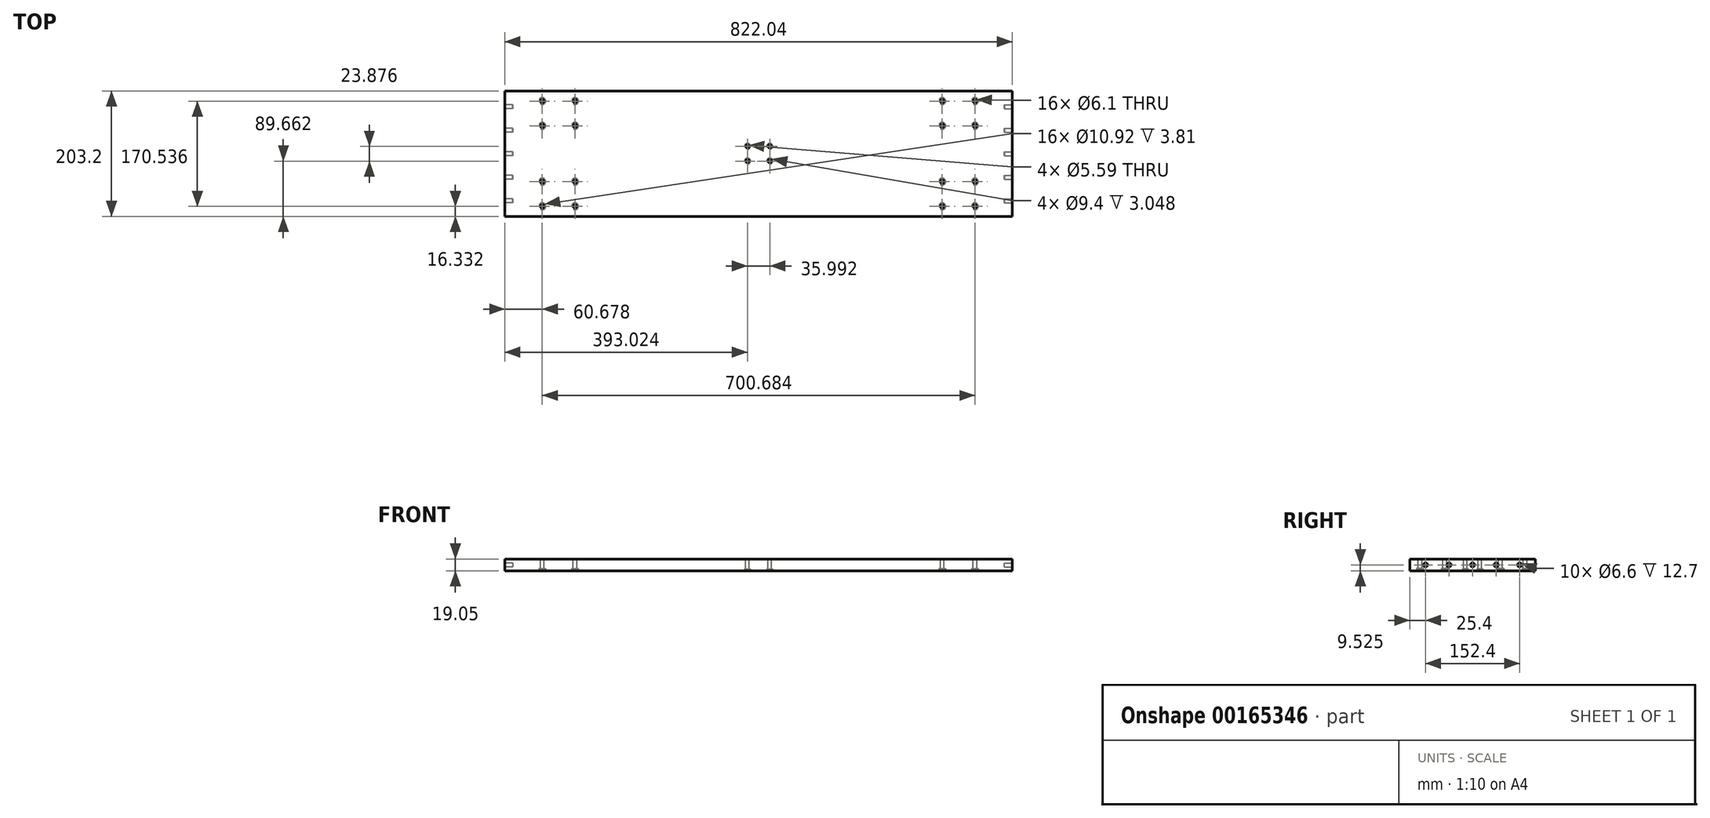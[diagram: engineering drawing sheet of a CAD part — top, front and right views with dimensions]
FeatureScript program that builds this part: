
annotation { "Feature Type Name" : "Feature", "Feature Type Description" : "" }
export const myFeature = defineFeature(function(context is Context, id is Id, definition is map)
    precondition{}
    {
        {
            var Q0;
            Q0=qCreatedBy(makeId("Top.planeOp"),FACE);
            var sketch = newSketch(context, id + "F0", { "sketchPlane" : qUnion([Q0])});
            skLineSegment(sketch, "E0.rect.bottom", {"start": v(411.02, -101.6) * mm, "end": v(-411.02, -101.6) * mm});
            skLineSegment(sketch, "E0.rect.top", {"start": v(411.02, 101.6) * mm, "end": v(-411.02, 101.6) * mm});
            skLineSegment(sketch, "E0.rect.left", {"start": v(411.02, -101.6) * mm, "end": v(411.02, 101.6) * mm});
            skLineSegment(sketch, "E0.rect.right", {"start": v(-411.02, -101.6) * mm, "end": v(-411.02, 101.6) * mm});
            skPoint(sketch, "E0.rect.middle", {"position": v(0, 0) * mm});
            skSolve(sketch);
        }
        {
            var Q0;
            Q0=qSketchRegion(id+"F0",true);
            extrude(context, id + "F1", {"entities" : qUnion([Q0]), "depth" : 19.05 * mm});
        }
        {
            var Q0;
            Q0=makeQuery(id+"F1.opExtrude","CAP_FACE",FACE,{"disambiguationData":[OSD([sQuery(id+"F0.wireOp",EDGE,"E0.rect.bottom"),sQuery(id+"F0.wireOp",EDGE,"E0.rect.top"),sQuery(id+"F0.wireOp",EDGE,"E0.rect.left"),sQuery(id+"F0.wireOp",EDGE,"E0.rect.right")])],"isStart":false});
            var sketch = newSketch(context, id + "F2", { "sketchPlane" : qUnion([Q0])});
            skLineSegment(sketch, "E1", {"start": v(-411.02, 85.27) * mm, "end": v(411.02, 85.27) * mm, "construction": true});
            skLineSegment(sketch, "E2", {"start": v(-411.02, 45.26) * mm, "end": v(411.02, 45.26) * mm, "construction": true});
            skLineSegment(sketch, "E3", {"start": v(-411.02, -45.26) * mm, "end": v(411.02, -45.26) * mm, "construction": true});
            skLineSegment(sketch, "E4", {"start": v(-411.02, -85.27) * mm, "end": v(411.02, -85.27) * mm, "construction": true});
            skLineSegment(sketch, "E5", {"start": v(411.02, -85.27) * mm, "end": v(412.08, -88.18) * mm, "construction": true});
            skLineSegment(sketch, "E6", {"start": v(-350.34, 101.6) * mm, "end": v(-350.34, -101.6) * mm, "construction": true});
            skLineSegment(sketch, "E7", {"start": v(-297.33, 101.6) * mm, "end": v(-297.33, -101.6) * mm, "construction": true});
            skLineSegment(sketch, "E8", {"start": v(-297.33, -101.6) * mm, "end": v(-294.42, -102.76) * mm, "construction": true});
            skLineSegment(sketch, "E9", {"start": v(297.33, 101.6) * mm, "end": v(297.33, -101.6) * mm, "construction": true});
            skLineSegment(sketch, "E10", {"start": v(350.34, 101.6) * mm, "end": v(350.34, -101.6) * mm, "construction": true});
            skCircle(sketch, "E11", {"center": v(-350.34, 85.27) * mm, "radius": 3.05 * mm});
            skCircle(sketch, "E12", {"center": v(-297.33, 85.27) * mm, "radius": 3.05 * mm});
            skCircle(sketch, "E13", {"center": v(-350.34, 45.26) * mm, "radius": 3.05 * mm});
            skCircle(sketch, "E14", {"center": v(-297.33, 45.26) * mm, "radius": 3.05 * mm});
            skCircle(sketch, "E15", {"center": v(-350.34, -45.26) * mm, "radius": 3.05 * mm});
            skCircle(sketch, "E16", {"center": v(-297.33, -45.26) * mm, "radius": 3.05 * mm});
            skCircle(sketch, "E17", {"center": v(297.33, 85.27) * mm, "radius": 3.05 * mm});
            skCircle(sketch, "E18", {"center": v(350.34, 85.27) * mm, "radius": 3.05 * mm});
            skCircle(sketch, "E19", {"center": v(297.33, 45.26) * mm, "radius": 3.05 * mm});
            skCircle(sketch, "E20", {"center": v(350.34, 45.26) * mm, "radius": 3.05 * mm});
            skCircle(sketch, "E21", {"center": v(297.33, -45.26) * mm, "radius": 3.05 * mm});
            skCircle(sketch, "E22", {"center": v(350.34, -45.26) * mm, "radius": 3.05 * mm});
            skCircle(sketch, "E23", {"center": v(297.33, -85.27) * mm, "radius": 3.05 * mm});
            skCircle(sketch, "E24", {"center": v(350.34, -85.27) * mm, "radius": 3.05 * mm});
            skCircle(sketch, "E25", {"center": v(-350.34, -85.27) * mm, "radius": 3.05 * mm});
            skCircle(sketch, "E26", {"center": v(-297.33, -85.27) * mm, "radius": 3.05 * mm});
            skSolve(sketch);
        }
        {
            var Q0;
            Q0=qSketchRegion(id+"F2",true);
            extrude(context, id + "F3", {"entities" : qUnion([Q0]), "operationType" : NewBodyOperationType.REMOVE, "endBound" : BoundingType.THROUGH_ALL, "oppositeDirection" : true, "depth" : 25.4 * mm});
        }
        {
            var Q0;
            Q0=makeQuery(id+"F1.opExtrude","CAP_FACE",FACE,{"disambiguationData":[OSD([sQuery(id+"F0.wireOp",EDGE,"E0.rect.bottom"),sQuery(id+"F0.wireOp",EDGE,"E0.rect.top"),sQuery(id+"F0.wireOp",EDGE,"E0.rect.left"),sQuery(id+"F0.wireOp",EDGE,"E0.rect.right")])],"isStart":false});
            var sketch = newSketch(context, id + "F4", { "sketchPlane" : qUnion([Q0])});
            skLineSegment(sketch, "E27.rect.bottom", {"start": v(-18, -11.94) * mm, "end": v(18, -11.94) * mm, "construction": true});
            skLineSegment(sketch, "E27.rect.top", {"start": v(-18, 11.94) * mm, "end": v(18, 11.94) * mm, "construction": true});
            skLineSegment(sketch, "E27.rect.left", {"start": v(-18, -11.94) * mm, "end": v(-18, 11.94) * mm, "construction": true});
            skLineSegment(sketch, "E27.rect.right", {"start": v(18, -11.94) * mm, "end": v(18, 11.94) * mm, "construction": true});
            skPoint(sketch, "E27.rect.middle", {"position": v(0, 0) * mm});
            skCircle(sketch, "E28", {"center": v(-18, 11.94) * mm, "radius": 2.8 * mm});
            skCircle(sketch, "E29", {"center": v(18, 11.94) * mm, "radius": 2.8 * mm});
            skCircle(sketch, "E30", {"center": v(-18, -11.94) * mm, "radius": 2.8 * mm});
            skCircle(sketch, "E31", {"center": v(18, -11.94) * mm, "radius": 2.8 * mm});
            skSolve(sketch);
        }
        {
            var Q0;
            Q0=qSketchRegion(id+"F4",true);
            extrude(context, id + "F5", {"entities" : qUnion([Q0]), "operationType" : NewBodyOperationType.REMOVE, "endBound" : BoundingType.THROUGH_ALL, "oppositeDirection" : true, "depth" : 25.4 * mm});
        }
        {
            var Q0;
            Q0=makeQuery(id+"F1.opExtrude","SWEPT_FACE",FACE,{"disambiguationData":[OSD([sQuery(id+"F0.wireOp",EDGE,"E0.rect.left")])]});
            var sketch = newSketch(context, id + "F6", { "sketchPlane" : qUnion([Q0])});
            skLineSegment(sketch, "E32", {"start": v(-101.6, 9.53) * mm, "end": v(101.6, 9.53) * mm, "construction": true});
            skLineSegment(sketch, "E33", {"start": v(-76.2, 19.05) * mm, "end": v(-76.2, 0) * mm, "construction": true});
            skLineSegment(sketch, "E34", {"start": v(-38.1, 19.05) * mm, "end": v(-38.1, 0) * mm, "construction": true});
            skLineSegment(sketch, "E35", {"start": v(0, 19.05) * mm, "end": v(0, 0) * mm, "construction": true});
            skLineSegment(sketch, "E36", {"start": v(38.1, 19.05) * mm, "end": v(38.1, 0) * mm, "construction": true});
            skLineSegment(sketch, "E37", {"start": v(76.2, 19.05) * mm, "end": v(76.2, 0) * mm, "construction": true});
            skCircle(sketch, "E38", {"center": v(-76.2, 9.53) * mm, "radius": 3.3 * mm});
            skCircle(sketch, "E39", {"center": v(-38.1, 9.52) * mm, "radius": 3.3 * mm});
            skCircle(sketch, "E40", {"center": v(0, 9.53) * mm, "radius": 3.3 * mm});
            skCircle(sketch, "E41", {"center": v(38.1, 9.53) * mm, "radius": 3.3 * mm});
            skCircle(sketch, "E42", {"center": v(76.2, 9.53) * mm, "radius": 3.3 * mm});
            skSolve(sketch);
        }
        {
            var Q0;
            Q0=qSketchRegion(id+"F6",true);
            extrude(context, id + "F7", {"entities" : qUnion([Q0]), "operationType" : NewBodyOperationType.REMOVE, "oppositeDirection" : true, "depth" : 12.7 * mm});
        }
        {
            var Q0;
            Q0=makeQuery(id+"F1.opExtrude","SWEPT_FACE",FACE,{"disambiguationData":[OSD([sQuery(id+"F0.wireOp",EDGE,"E0.rect.right")])]});
            var sketch = newSketch(context, id + "F8", { "sketchPlane" : qUnion([Q0])});
            skLineSegment(sketch, "E43", {"start": v(-101.6, 9.53) * mm, "end": v(101.6, 9.53) * mm, "construction": true});
            skLineSegment(sketch, "E44", {"start": v(-76.2, 19.05) * mm, "end": v(-76.2, 0) * mm, "construction": true});
            skLineSegment(sketch, "E45", {"start": v(-38.1, 19.05) * mm, "end": v(-38.1, 0) * mm, "construction": true});
            skLineSegment(sketch, "E46", {"start": v(0, 19.05) * mm, "end": v(0, 0) * mm, "construction": true});
            skLineSegment(sketch, "E47", {"start": v(38.1, 19.05) * mm, "end": v(38.1, 0) * mm, "construction": true});
            skLineSegment(sketch, "E48", {"start": v(76.2, 19.05) * mm, "end": v(76.2, 0) * mm, "construction": true});
            skCircle(sketch, "E49", {"center": v(-76.2, 9.52) * mm, "radius": 3.3 * mm});
            skCircle(sketch, "E50", {"center": v(-38.1, 9.52) * mm, "radius": 3.3 * mm});
            skCircle(sketch, "E51", {"center": v(0, 9.53) * mm, "radius": 3.3 * mm});
            skCircle(sketch, "E52", {"center": v(38.1, 9.53) * mm, "radius": 3.3 * mm});
            skCircle(sketch, "E53", {"center": v(76.2, 9.53) * mm, "radius": 3.3 * mm});
            skSolve(sketch);
        }
        {
            var Q0;
            Q0=qSketchRegion(id+"F8",true);
            extrude(context, id + "F9", {"entities" : qUnion([Q0]), "operationType" : NewBodyOperationType.REMOVE, "oppositeDirection" : true, "depth" : 12.7 * mm});
        }
        {
            var Q0;
            Q0=makeQuery(id+"F1.opExtrude","CAP_FACE",FACE,{"disambiguationData":[OSD([sQuery(id+"F0.wireOp",EDGE,"E0.rect.bottom"),sQuery(id+"F0.wireOp",EDGE,"E0.rect.top"),sQuery(id+"F0.wireOp",EDGE,"E0.rect.left"),sQuery(id+"F0.wireOp",EDGE,"E0.rect.right")])],"isStart":true});
            var sketch = newSketch(context, id + "F10", { "sketchPlane" : qUnion([Q0])});
            skCircle(sketch, "E54", {"center": v(-350.34, 85.27) * mm, "radius": 5.46 * mm});
            skCircle(sketch, "E55", {"center": v(-350.34, 45.26) * mm, "radius": 5.46 * mm});
            skCircle(sketch, "E56", {"center": v(-297.33, 85.27) * mm, "radius": 5.46 * mm});
            skCircle(sketch, "E57", {"center": v(-297.33, 45.26) * mm, "radius": 5.46 * mm});
            skCircle(sketch, "E58", {"center": v(-350.34, -45.26) * mm, "radius": 5.46 * mm});
            skCircle(sketch, "E59", {"center": v(-297.33, -45.26) * mm, "radius": 5.46 * mm});
            skCircle(sketch, "E60", {"center": v(-297.33, -85.27) * mm, "radius": 5.46 * mm});
            skCircle(sketch, "E61", {"center": v(-350.34, -85.27) * mm, "radius": 5.46 * mm});
            skCircle(sketch, "E62", {"center": v(297.33, 85.27) * mm, "radius": 5.46 * mm});
            skCircle(sketch, "E63", {"center": v(297.33, 45.26) * mm, "radius": 5.46 * mm});
            skCircle(sketch, "E64", {"center": v(350.34, 85.27) * mm, "radius": 5.46 * mm});
            skCircle(sketch, "E65", {"center": v(350.34, 45.26) * mm, "radius": 5.46 * mm});
            skCircle(sketch, "E66", {"center": v(297.33, -45.26) * mm, "radius": 5.46 * mm});
            skCircle(sketch, "E67", {"center": v(297.33, -85.27) * mm, "radius": 5.46 * mm});
            skCircle(sketch, "E68", {"center": v(350.34, -45.26) * mm, "radius": 5.46 * mm});
            skCircle(sketch, "E69", {"center": v(350.34, -85.27) * mm, "radius": 5.46 * mm});
            skSolve(sketch);
        }
        {
            var Q0;
            Q0 = qSketchRegion(id + "F10", true);
            extrude(context, id + "F11", {"entities" : qUnion([Q0]), "operationType" : NewBodyOperationType.REMOVE, "oppositeDirection" : true, "depth" : 3.8 * mm});
        }
        {
            var Q0;
            Q0=makeQuery(id+"F1.opExtrude","CAP_FACE",FACE,{"disambiguationData":[OSD([sQuery(id+"F0.wireOp",EDGE,"E0.rect.bottom"),sQuery(id+"F0.wireOp",EDGE,"E0.rect.top"),sQuery(id+"F0.wireOp",EDGE,"E0.rect.left"),sQuery(id+"F0.wireOp",EDGE,"E0.rect.right")])],"isStart":true});
            var sketch = newSketch(context, id + "F12", { "sketchPlane" : qUnion([Q0])});
            skCircle(sketch, "E70", {"center": v(-18, 11.94) * mm, "radius": 4.7 * mm});
            skCircle(sketch, "E71", {"center": v(-18, -11.94) * mm, "radius": 4.7 * mm});
            skCircle(sketch, "E72", {"center": v(18, -11.94) * mm, "radius": 4.7 * mm});
            skCircle(sketch, "E73", {"center": v(18, 11.94) * mm, "radius": 4.7 * mm});
            skSolve(sketch);
        }
        {
            var Q0;
            Q0 = qSketchRegion(id + "F12", true);
            extrude(context, id + "F13", {"entities" : qUnion([Q0]), "operationType" : NewBodyOperationType.REMOVE, "oppositeDirection" : true, "depth" : 3.05 * mm});
        }
    });
